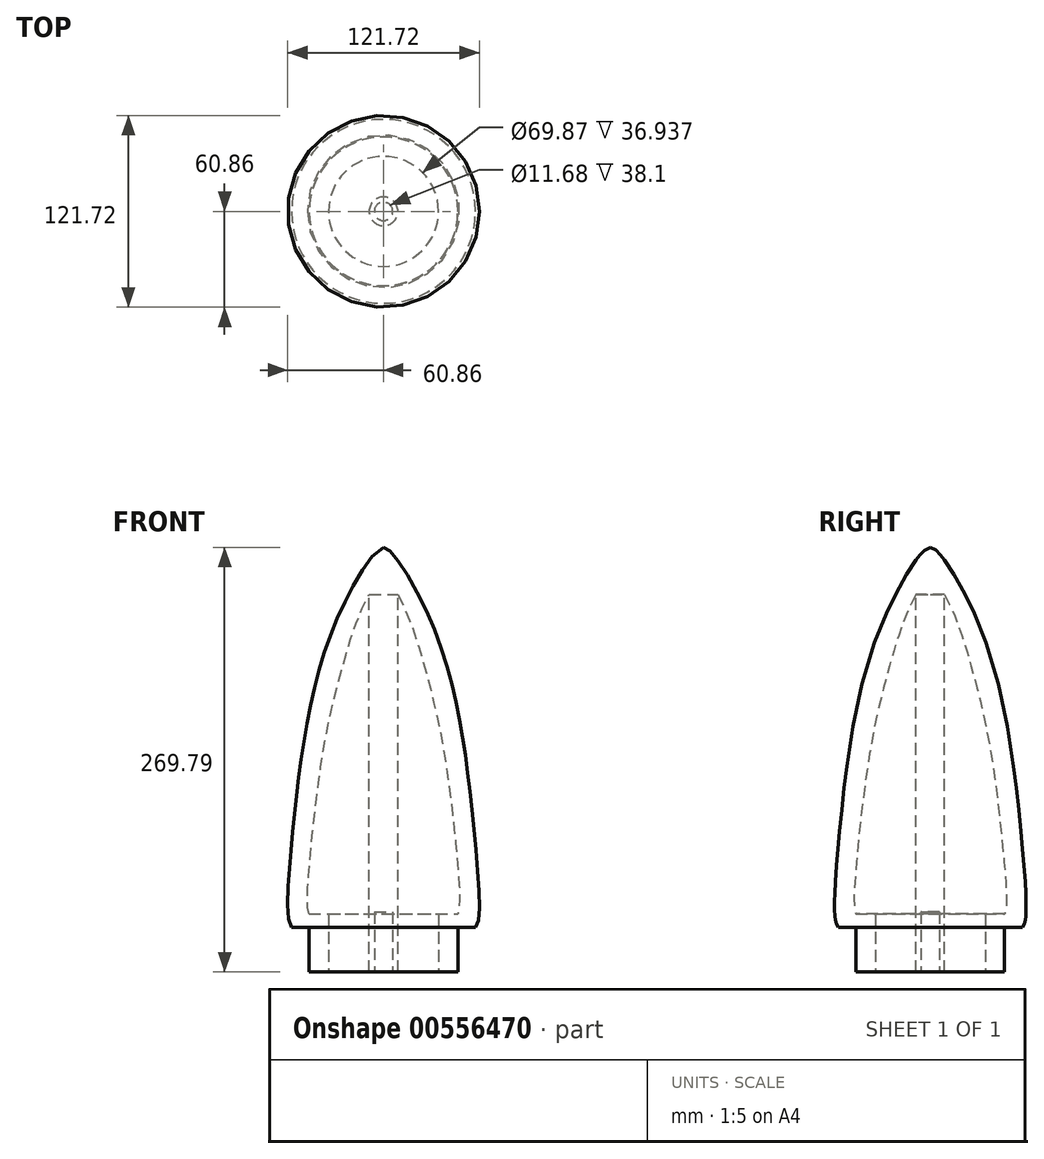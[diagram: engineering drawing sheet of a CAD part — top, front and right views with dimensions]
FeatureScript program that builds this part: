
annotation { "Feature Type Name" : "Feature", "Feature Type Description" : "" }
export const myFeature = defineFeature(function(context is Context, id is Id, definition is map)
    precondition{}
    {
        {
            var Q0;
            Q0=qCreatedBy(makeId("Front.planeOp"),FACE);
            var sketch = newSketch(context, id + "F0", { "sketchPlane" : qUnion([Q0])});
            skLineSegment(sketch, "E0", {"start": v(0, 0) * mm, "end": v(47.2, 0) * mm});
            skLineSegment(sketch, "E1", {"start": v(47.2, 0) * mm, "end": v(47.2, 28.47) * mm});
            skLineSegment(sketch, "E2", {"start": v(47.2, 28.47) * mm, "end": v(58.42, 28.47) * mm});
            skLineSegment(sketch, "E3", {"start": v(0, 0) * mm, "end": v(0, 269.79) * mm});
            skFitSpline(sketch, "E4", {"points": [v(58.42, 28.47) * mm, v(58.42, 80.63) * mm, v(49.22, 154.64) * mm, v(28.28, 226.96) * mm, v(0, 269.79) * mm], "startDerivative": vector(55.75, 42.45) * mm, "endDerivative": vector(-76.99, 3.58) * mm});
            skSolve(sketch);
        }
        {
            var Q0;
            Q0 = qSketchRegion(id + "F0", true);
            var Q1;
            Q1=sQuery(id+"F0.wireOp",EDGE,"E3");
            revolve(context, id + "F1", {"entities" : qUnion([Q0]), "axis" : qUnion([Q1]), "revolveType" : RevolveType.FULL});
        }
        {
            var Q0;
            Q0=qCreatedBy(makeId("Right.planeOp"),FACE);
            var sketch = newSketch(context, id + "F2", { "sketchPlane" : qUnion([Q0])});
            skLineSegment(sketch, "E5", {"start": v(0, 0) * mm, "end": v(34.93, 0) * mm});
            skLineSegment(sketch, "E6", {"start": v(34.93, 0) * mm, "end": v(34.93, 28.4) * mm});
            skLineSegment(sketch, "E7", {"start": v(34.93, 28.4) * mm, "end": v(34.93, 36.94) * mm});
            skLineSegment(sketch, "E8", {"start": v(34.93, 36.94) * mm, "end": v(47.33, 36.94) * mm});
            skFitSpline(sketch, "E9", {"points": [v(47.33, 36.94) * mm, v(47.33, 65.14) * mm, v(39.16, 134.86) * mm, v(27.1, 189.99) * mm, v(0, 252.3) * mm], "startDerivative": vector(28.49, 85.46) * mm, "endDerivative": vector(-140.62, 141.8) * mm});
            skLineSegment(sketch, "E10", {"start": v(0, 252.3) * mm, "end": v(0, 0) * mm});
            skSolve(sketch);
        }
        {
            var Q0;
            Q0 = qSketchRegion(id + "F2", true);
            var Q1;
            Q1=sQuery(id+"F2.wireOp",EDGE,"E10");
            revolve(context, id + "F3", {"operationType" : NewBodyOperationType.REMOVE, "entities" : qUnion([Q0]), "axis" : qUnion([Q1]), "revolveType" : RevolveType.FULL, "oppositeDirection" : true});
        }
        {
            var Q0;
            Q0=qCreatedBy(makeId("Top.planeOp"),FACE);
            cPlane(context, id + "F4", {"entities" : qUnion([Q0]), "cplaneType" : CPlaneType.OFFSET, "offset" : 254 * mm, "width" : 152.4 * mm, "height" : 152.4 * mm});
        }
        {
            var Q0;
            Q0=qCreatedBy(id+"F4.planeOp",FACE);
            var sketch = newSketch(context, id + "F5", { "sketchPlane" : qUnion([Q0])});
            skPoint(sketch, "E11", {"position": v(0, 0) * mm});
            skCircle(sketch, "E12", {"center": v(0, 0) * mm, "radius": 9.1 * mm});
            skSolve(sketch);
        }
        {
            var Q0;
            Q0 = qSketchRegion(id + "F5", true);
            var Q1;
            Q1=makeQuery(id+"F1.opRevolve","SWEPT_FACE",FACE,{"disambiguationData":[OSD([sQuery(id+"F0.wireOp",EDGE,"E0")])]});
            extrude(context, id + "F6", {"entities" : qUnion([Q0]), "operationType" : NewBodyOperationType.ADD, "endBound" : BoundingType.UP_TO_SURFACE, "oppositeDirection" : true, "depth" : 203.2 * mm, "endBoundEntityFace" : qUnion([Q1]), "offsetDistance" : 25.4 * mm});
        }
        {
            var Q0;
            Q0=makeQuery(id+"F6.opExtrude","CAP_FACE",FACE,{"disambiguationData":[OSD([sQuery(id+"F5.wireOp",EDGE,"E12")])],"isStart":false});
            var sketch = newSketch(context, id + "F7", { "sketchPlane" : qUnion([Q0])});
            skCircle(sketch, "E13", {"center": v(0, 0) * mm, "radius": 5.84 * mm});
            skSolve(sketch);
        }
        {
            var Q0;
            Q0 = qSketchRegion(id + "F7", true);
            extrude(context, id + "F8", {"entities" : qUnion([Q0]), "operationType" : NewBodyOperationType.REMOVE, "oppositeDirection" : true, "depth" : 38.1 * mm, "offsetDistance" : 25.4 * mm});
        }
    });
